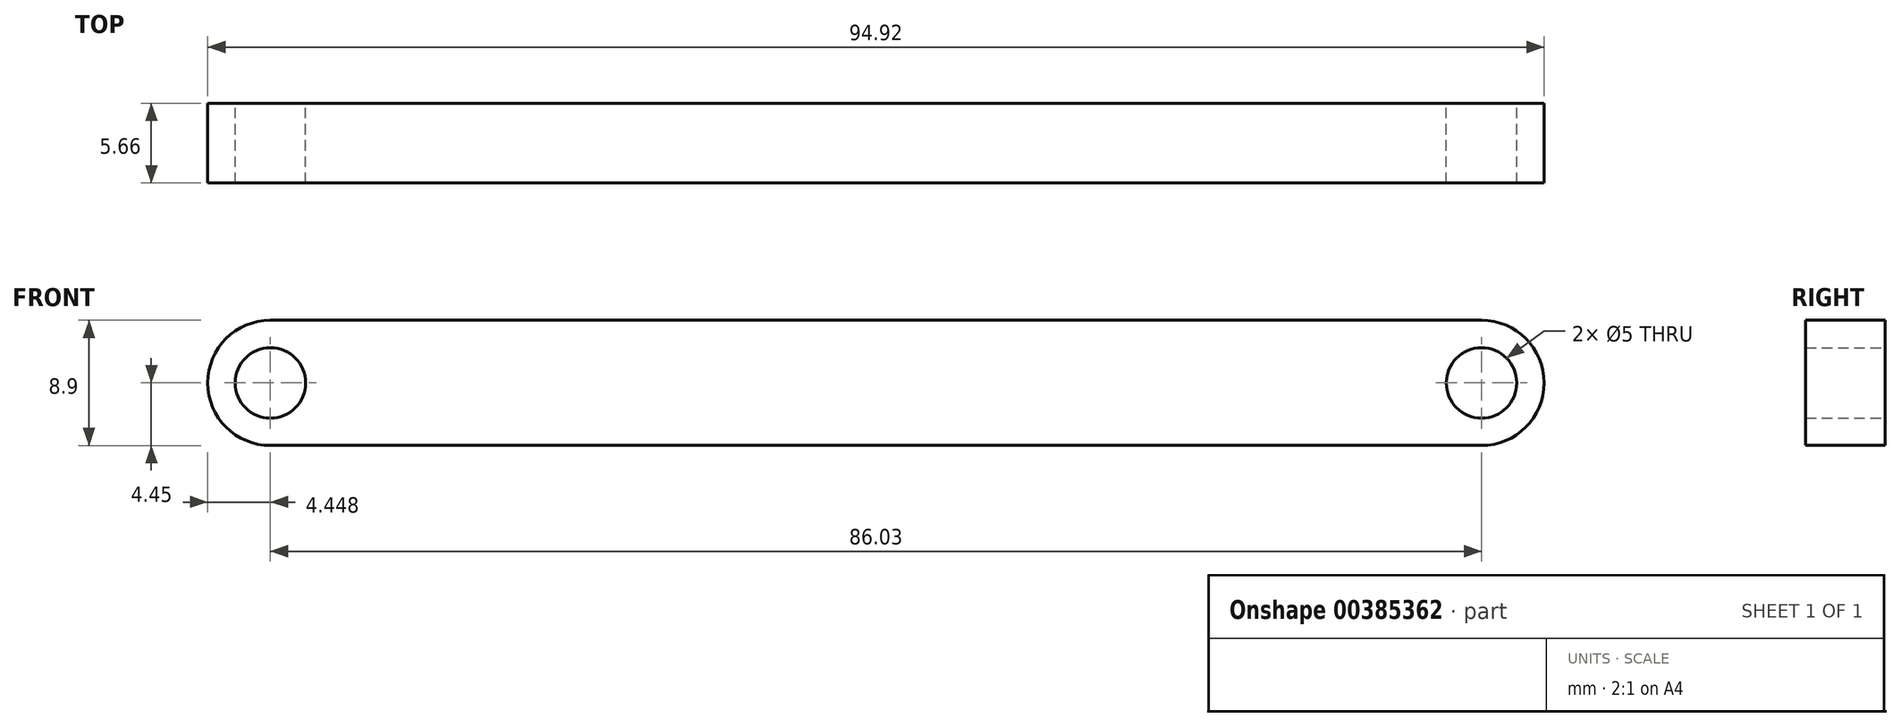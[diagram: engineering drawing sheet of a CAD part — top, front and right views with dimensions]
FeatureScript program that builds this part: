
annotation { "Feature Type Name" : "Feature", "Feature Type Description" : "" }
export const myFeature = defineFeature(function(context is Context, id is Id, definition is map)
    precondition{}
    {
        {
            var Q0;
            Q0=qCreatedBy(makeId("Front.planeOp"),FACE);
            var sketch = newSketch(context, id + "F0", { "sketchPlane" : qUnion([Q0])});
            skCircle(sketch, "E0", {"center": v(-17.28, 0) * mm, "radius": 2.5 * mm});
            skCircle(sketch, "E1", {"center": v(68.75, 0) * mm, "radius": 2.5 * mm});
            skArc(sketch, "E2", {"start": v(-17.28, 4.45) * mm, "mid": v(-21.73, 0) * mm, "end": v(-17.28, -4.45) * mm});
            skArc(sketch, "E3", {"start": v(68.75, -4.44) * mm, "mid": v(73.2, 0) * mm, "end": v(68.75, 4.45) * mm});
            skLineSegment(sketch, "E4", {"start": v(-17.28, 4.44) * mm, "end": v(68.75, 4.45) * mm});
            skLineSegment(sketch, "E5", {"start": v(-17.28, -4.45) * mm, "end": v(68.75, -4.44) * mm});
            skSolve(sketch);
        }
        {
            var Q0;
            Q0=makeQuery(id+"F0.imprint","IMPRINT",FACE,{"disambiguationData":[TD([[makeQuery(id+"F0.imprint","IMPRINT",EDGE,{"derivedFrom":sQuery(id+"F0.wireOp",EDGE,"E0")}),-1.0]])]});
            extrude(context, id + "F1", {"entities" : qUnion([Q0]), "depth" : 5.66 * mm});
        }
    });
